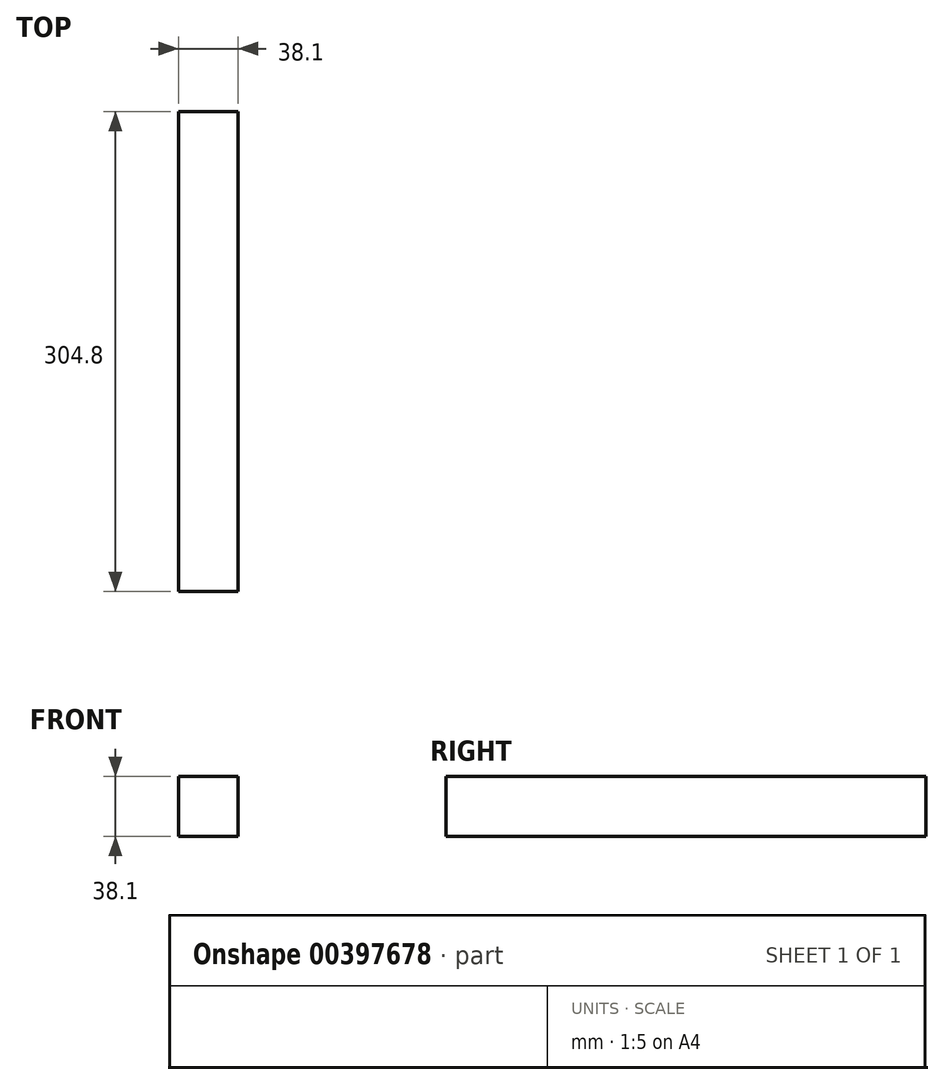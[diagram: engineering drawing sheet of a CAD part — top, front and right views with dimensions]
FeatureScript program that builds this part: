
annotation { "Feature Type Name" : "Feature", "Feature Type Description" : "" }
export const myFeature = defineFeature(function(context is Context, id is Id, definition is map)
    precondition{}
    {
        {
            var Q0;
            Q0=qCreatedBy(makeId("Front.planeOp"),FACE);
            var sketch = newSketch(context, id + "F0", { "sketchPlane" : qUnion([Q0])});
            skLineSegment(sketch, "E0.bottom", {"start": v(0, 0) * mm, "end": v(38.1, 0) * mm});
            skLineSegment(sketch, "E0.top", {"start": v(0, 38.1) * mm, "end": v(38.1, 38.1) * mm});
            skLineSegment(sketch, "E0.left", {"start": v(0, 0) * mm, "end": v(0, 38.1) * mm});
            skLineSegment(sketch, "E0.right", {"start": v(38.1, 0) * mm, "end": v(38.1, 38.1) * mm});
            skSolve(sketch);
        }
        {
            var Q0;
            Q0=makeQuery(id+"F0.imprint","IMPRINT",FACE,{"disambiguationData":[TD([[makeQuery(id+"F0.imprint","IMPRINT",EDGE,{"derivedFrom":sQuery(id+"F0.wireOp",EDGE,"E0.bottom")}),1.0]])]});
            extrude(context, id + "F1", {"entities" : qUnion([Q0]), "depth" : 304.8 * mm, "offsetDistance" : 25.4 * mm});
        }
    });
